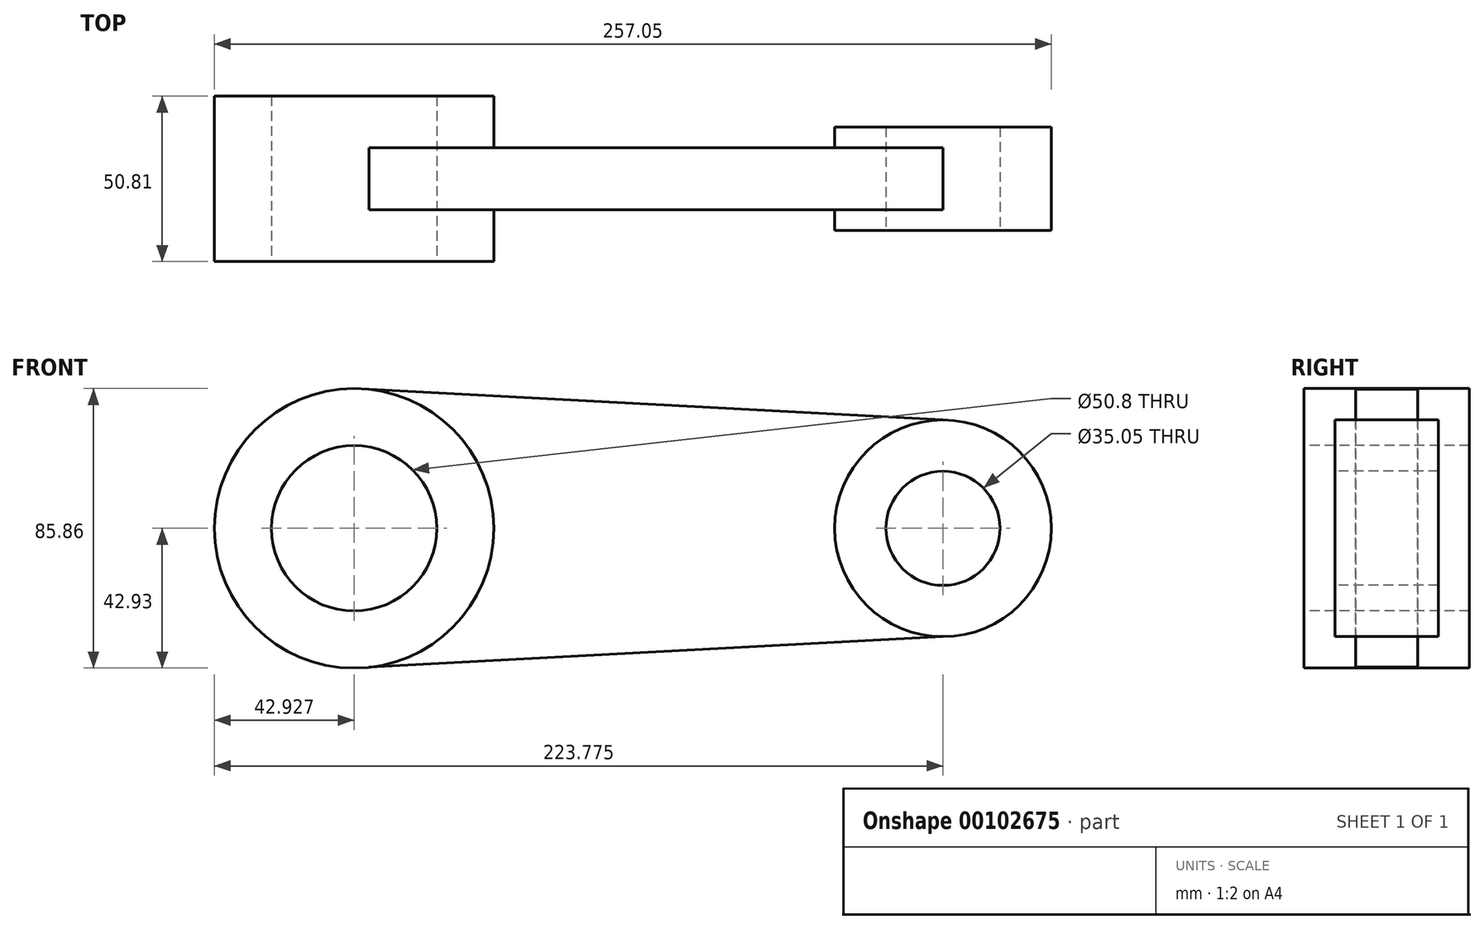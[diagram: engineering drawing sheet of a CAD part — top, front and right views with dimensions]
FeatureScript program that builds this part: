
annotation { "Feature Type Name" : "Feature", "Feature Type Description" : "" }
export const myFeature = defineFeature(function(context is Context, id is Id, definition is map)
    precondition{}
    {
        {
            var Q0;
            Q0=qCreatedBy(makeId("Front.planeOp"),FACE);
            var sketch = newSketch(context, id + "F0", { "sketchPlane" : qUnion([Q0])});
            skCircle(sketch, "E0", {"center": v(-57.88, 0) * mm, "radius": 42.93 * mm});
            skCircle(sketch, "E1", {"center": v(122.97, 0) * mm, "radius": 33.27 * mm});
            skLineSegment(sketch, "E2", {"start": v(-57.88, 42.93) * mm, "end": v(122.97, 33.27) * mm});
            skLineSegment(sketch, "E3", {"start": v(122.97, -33.27) * mm, "end": v(-57.88, -42.93) * mm});
            skSolve(sketch);
        }
        {
            var Q0;
            Q0 = qSketchRegion(id + "F0", true);
            extrude(context, id + "F1", {"entities" : qUnion([Q0]), "oppositeDirection" : true, "depth" : 19.05 * mm});
        }
        {
            var Q0;
            Q0=makeQuery(id+"F1.opExtrude","CAP_FACE",FACE,{"disambiguationData":[OSD([sQuery(id+"F0.wireOp",EDGE,"E0"),sQuery(id+"F0.wireOp",EDGE,"E1"),sQuery(id+"F0.wireOp",EDGE,"E2"),sQuery(id+"F0.wireOp",EDGE,"E3")])],"isStart":false});
            var sketch = newSketch(context, id + "F2", { "sketchPlane" : qUnion([Q0])});
            skCircle(sketch, "E4", {"center": v(57.88, 0) * mm, "radius": 42.93 * mm});
            skSolve(sketch);
        }
        {
            var Q0;
            Q0 = qSketchRegion(id + "F2", true);
            extrude(context, id + "F3", {"entities" : qUnion([Q0]), "operationType" : NewBodyOperationType.ADD, "depth" : 15.88 * mm});
        }
        {
            var Q0;
            {var subQ0=sQuery(id+"F0.wireOp",EDGE,"E3");var subQ1=sQuery(id+"F0.wireOp",EDGE,"E2");var subQ3=sQuery(id+"F0.wireOp",EDGE,"E1");Q0=makeQuery(id+"FoTDxnYgHq18ZZF_1.boolean.opBoolean","SPLIT",FACE,{"disambiguationData":[TD([makeQuery(id+"F1.opExtrude","SWEPT_FACE",FACE,{"disambiguationData":[OSD([subQ3])]})])],"derivedFrom":makeQuery(id+"F1.opExtrude","CAP_FACE",FACE,{"disambiguationData":[OSD([sQuery(id+"F0.wireOp",EDGE,"E0"),subQ3,subQ1,subQ0])],"isStart":true})});}
            var sketch = newSketch(context, id + "F4", { "sketchPlane" : qUnion([Q0])});
            skCircle(sketch, "E5", {"center": v(122.97, 0) * mm, "radius": 33.27 * mm});
            skSolve(sketch);
        }
        {
            var Q0;
            Q0 = qSketchRegion(id + "F4", true);
            extrude(context, id + "F5", {"entities" : qUnion([Q0]), "operationType" : NewBodyOperationType.ADD, "depth" : 6.35 * mm});
        }
        {
            var Q0;
            Q0=makeQuery(id+"F1.opExtrude","CAP_FACE",FACE,{"disambiguationData":[OSD([sQuery(id+"F0.wireOp",EDGE,"E0"),sQuery(id+"F0.wireOp",EDGE,"E1"),sQuery(id+"F0.wireOp",EDGE,"E2"),sQuery(id+"F0.wireOp",EDGE,"E3")])],"isStart":false});
            var sketch = newSketch(context, id + "F6", { "sketchPlane" : qUnion([Q0])});
            skCircle(sketch, "E6", {"center": v(-122.97, 0) * mm, "radius": 33.27 * mm});
            skSolve(sketch);
        }
        {
            var Q0;
            Q0 = qSketchRegion(id + "F6", true);
            extrude(context, id + "F7", {"entities" : qUnion([Q0]), "operationType" : NewBodyOperationType.ADD, "depth" : 6.35 * mm});
        }
        {
            var Q0;
            Q0=makeQuery(id+"F1.opExtrude","CAP_FACE",FACE,{"disambiguationData":[OSD([sQuery(id+"F0.wireOp",EDGE,"E0"),sQuery(id+"F0.wireOp",EDGE,"E1"),sQuery(id+"F0.wireOp",EDGE,"E2"),sQuery(id+"F0.wireOp",EDGE,"E3")])],"isStart":true});
            var sketch = newSketch(context, id + "F8", { "sketchPlane" : qUnion([Q0])});
            skCircle(sketch, "E7", {"center": v(-57.88, 0) * mm, "radius": 42.93 * mm});
            skSolve(sketch);
        }
        {
            var Q0;
            Q0 = qSketchRegion(id + "F8", true);
            extrude(context, id + "F9", {"entities" : qUnion([Q0]), "operationType" : NewBodyOperationType.ADD, "depth" : 15.88 * mm});
        }
        {
            var Q0;
            Q0=makeQuery(id+"F9.opExtrude","CAP_FACE",FACE,{"disambiguationData":[OSD([sQuery(id+"F8.wireOp",EDGE,"E7")])],"isStart":false});
            var sketch = newSketch(context, id + "F10", { "sketchPlane" : qUnion([Q0])});
            skCircle(sketch, "E8", {"center": v(-57.88, 0) * mm, "radius": 25.4 * mm});
            skSolve(sketch);
        }
        {
            var Q0;
            Q0 = qSketchRegion(id + "F10", true);
            extrude(context, id + "F11", {"entities" : qUnion([Q0]), "operationType" : NewBodyOperationType.REMOVE, "oppositeDirection" : true, "depth" : 50.8 * mm});
        }
        {
            var Q0;
            Q0=makeQuery(id+"F5.opExtrude","CAP_FACE",FACE,{"disambiguationData":[OSD([sQuery(id+"F4.wireOp",EDGE,"E5")])],"isStart":false});
            var sketch = newSketch(context, id + "F12", { "sketchPlane" : qUnion([Q0])});
            skCircle(sketch, "E9", {"center": v(122.97, 0) * mm, "radius": 17.53 * mm});
            skSolve(sketch);
        }
        {
            var Q0;
            Q0 = qSketchRegion(id + "F12", true);
            extrude(context, id + "F13", {"entities" : qUnion([Q0]), "operationType" : NewBodyOperationType.REMOVE, "oppositeDirection" : true, "depth" : 31.75 * mm});
        }
    });
